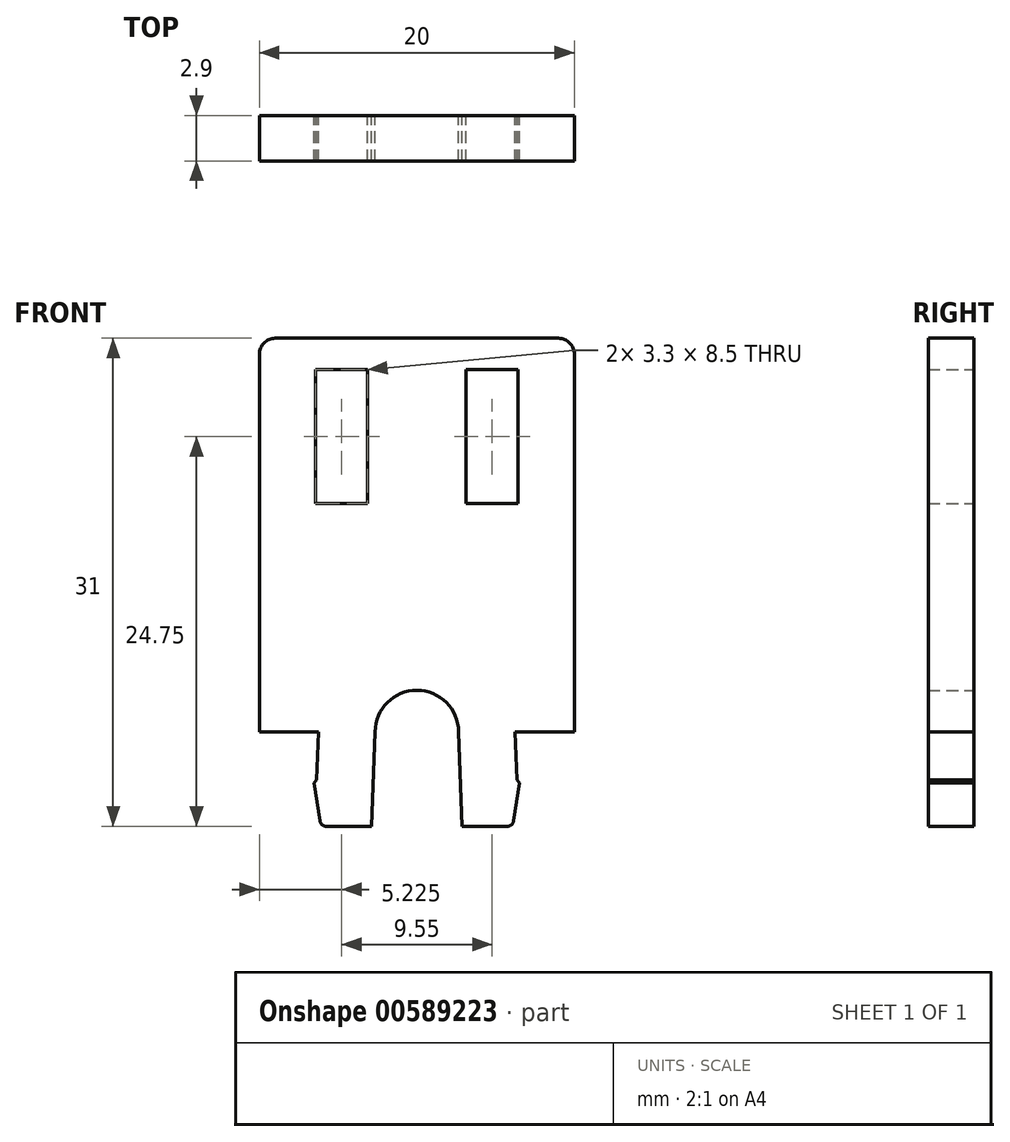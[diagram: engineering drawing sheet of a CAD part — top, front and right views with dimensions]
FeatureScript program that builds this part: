
annotation { "Feature Type Name" : "Feature", "Feature Type Description" : "" }
export const myFeature = defineFeature(function(context is Context, id is Id, definition is map)
    precondition{}
    {
        {
            var Q0;
            Q0=qCreatedBy(makeId("Front.planeOp"),FACE);
            var sketch = newSketch(context, id + "F0", { "sketchPlane" : qUnion([Q0])});
            skLineSegment(sketch, "E0.bottom", {"start": v(-10, 0) * mm, "end": v(-6.25, 0) * mm});
            skLineSegment(sketch, "E0.top", {"start": v(-9, 25) * mm, "end": v(9, 25) * mm});
            skLineSegment(sketch, "E0.left", {"start": v(-10, 0) * mm, "end": v(-10, 24) * mm});
            skLineSegment(sketch, "E0.right", {"start": v(10, 0) * mm, "end": v(10, 24) * mm});
            skPoint(sketch, "E0.middle", {"position": v(0, 12.5) * mm});
            skLineSegment(sketch, "E1.bottom", {"start": v(-6.42, 23) * mm, "end": v(-3.13, 23) * mm});
            skLineSegment(sketch, "E1.top", {"start": v(-6.42, 14.5) * mm, "end": v(-3.13, 14.5) * mm});
            skLineSegment(sketch, "E1.left", {"start": v(-6.42, 23) * mm, "end": v(-6.42, 14.5) * mm});
            skLineSegment(sketch, "E1.right", {"start": v(-3.12, 23) * mm, "end": v(-3.12, 14.5) * mm});
            skPoint(sketch, "E2.visualSharp", {"position": v(-10, 25) * mm});
            skArc(sketch, "E2.filletArc", {"start": v(-9, 25) * mm, "mid": v(-9.7, 24.7) * mm, "end": v(-10, 24) * mm});
            skPoint(sketch, "E3.visualSharp", {"position": v(10, 25) * mm});
            skArc(sketch, "E3.filletArc", {"start": v(10, 24) * mm, "mid": v(9.7, 24.7) * mm, "end": v(9, 25) * mm});
            skLineSegment(sketch, "E4.MirrorCS", {"start": v(3.12, 23) * mm, "end": v(3.12, 14.5) * mm});
            skLineSegment(sketch, "E5.MirrorCS", {"start": v(6.42, 23) * mm, "end": v(3.13, 23) * mm});
            skLineSegment(sketch, "E6.MirrorCS", {"start": v(6.42, 23) * mm, "end": v(6.42, 14.5) * mm});
            skLineSegment(sketch, "E7.MirrorCS", {"start": v(6.42, 14.5) * mm, "end": v(3.12, 14.5) * mm});
            skArc(sketch, "E8", {"start": v(-2.64, 0) * mm, "mid": v(0, 2.64) * mm, "end": v(2.64, 0) * mm});
            skLineSegment(sketch, "E9.trimOffspring", {"start": v(6.25, 0) * mm, "end": v(10, 0) * mm});
            skLineSegment(sketch, "E10", {"start": v(-2.88, -6) * mm, "end": v(-5.76, -6) * mm});
            skLineSegment(sketch, "E11", {"start": v(-6.15, -5.66) * mm, "end": v(-6.53, -3.25) * mm});
            skLineSegment(sketch, "E12", {"start": v(-6.53, -3.25) * mm, "end": v(-6.37, -3.05) * mm});
            skLineSegment(sketch, "E13", {"start": v(-6.37, -3.05) * mm, "end": v(-6.25, 0) * mm});
            skPoint(sketch, "E14.visualSharp", {"position": v(-6.1, -6) * mm});
            skArc(sketch, "E14.filletArc", {"start": v(-6.15, -5.66) * mm, "mid": v(-6.02, -5.9) * mm, "end": v(-5.76, -6) * mm});
            skArc(sketch, "E15.MirrorCS", {"start": v(6.15, -5.66) * mm, "mid": v(6.02, -5.9) * mm, "end": v(5.76, -6) * mm});
            skLineSegment(sketch, "E16.MirrorCS", {"start": v(6.53, -3.25) * mm, "end": v(6.37, -3.05) * mm});
            skLineSegment(sketch, "E17.MirrorCS", {"start": v(6.15, -5.66) * mm, "end": v(6.53, -3.25) * mm});
            skPoint(sketch, "E18.MirrorP", {"position": v(6.1, -6) * mm});
            skLineSegment(sketch, "E19.MirrorCS", {"start": v(2.88, -6) * mm, "end": v(5.76, -6) * mm});
            skLineSegment(sketch, "E20.MirrorCS", {"start": v(6.37, -3.05) * mm, "end": v(6.25, 0) * mm});
            skLineSegment(sketch, "E21", {"start": v(-2.64, 0) * mm, "end": v(-2.88, -6) * mm});
            skPoint(sketch, "E22.MirrorCS.start.orphan", {"position": v(2.64, 0) * mm});
            skLineSegment(sketch, "E23.MirrorCS", {"start": v(2.64, 0) * mm, "end": v(2.88, -6) * mm});
            skSolve(sketch);
        }
        {
            var Q0;
            Q0=makeQuery(id+"F0.imprint","IMPRINT",FACE,{"disambiguationData":[TD([[makeQuery(id+"F0.imprint","IMPRINT",EDGE,{"derivedFrom":sQuery(id+"F0.wireOp",EDGE,"E0.bottom")}),1.0]])]});
            extrude(context, id + "F1", {"entities" : qUnion([Q0]), "depth" : 2.9 * mm, "offsetDistance" : 25 * mm});
        }
    });
